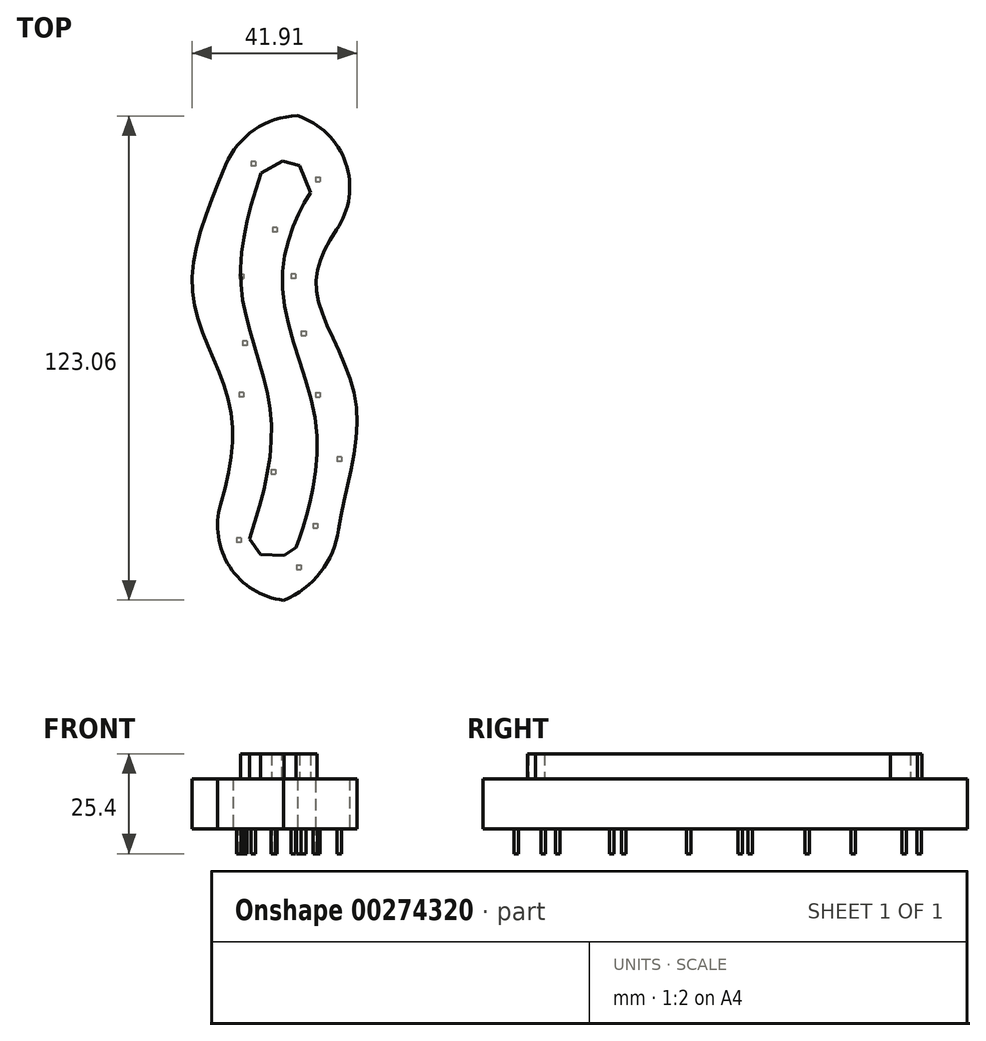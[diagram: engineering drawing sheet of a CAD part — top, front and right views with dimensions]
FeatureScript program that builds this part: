
annotation { "Feature Type Name" : "Feature", "Feature Type Description" : "" }
export const myFeature = defineFeature(function(context is Context, id is Id, definition is map)
    precondition{}
    {
        {
            var Q0;
            Q0=qCreatedBy(makeId("Top.planeOp"),FACE);
            var sketch = newSketch(context, id + "F0", { "sketchPlane" : qUnion([Q0])});
            skFitSpline(sketch, "E0", {"points": [v(-41.01, -54.79) * mm, v(-30.73, -10.92) * mm, v(-40.76, 21.76) * mm, v(-25.89, 69.26) * mm], "startDerivative": vector(46.92, 133.29) * mm, "endDerivative": vector(46.95, 139.93) * mm});
            skLineSegment(sketch, "E1", {"start": v(-25.89, 69.26) * mm, "end": v(10.42, 57.7) * mm});
            skFitSpline(sketch, "E2", {"points": [v(10.42, 57.7) * mm, v(-3.88, 36.84) * mm, v(-9.01, 19.64) * mm, v(0.92, -8.43) * mm, v(-3.91, -43.6) * mm, v(-2.91, -59.33) * mm], "startDerivative": vector(-38.98, -103.6) * mm, "endDerivative": vector(-24.02, -86.28) * mm});
            skLineSegment(sketch, "E3", {"start": v(-41.01, -54.79) * mm, "end": v(-2.91, -59.33) * mm});
            skSolve(sketch);
        }
        {
            var Q0;
            Q0=qCreatedBy(makeId("Top.planeOp"),FACE);
            var sketch = newSketch(context, id + "F1", { "sketchPlane" : qUnion([Q0])});
            skFitSpline(sketch, "E4", {"points": [v(-27.4, -45.76) * mm, v(-20.77, -10.84) * mm, v(-28.3, 21.68) * mm, v(-21.98, 55.1) * mm], "startDerivative": vector(33.82, 104.13) * mm, "endDerivative": vector(33.06, 101.43) * mm});
            skLineSegment(sketch, "E5", {"start": v(-27.4, -45.76) * mm, "end": v(-15.12, -46.35) * mm});
            skLineSegment(sketch, "E6", {"start": v(-21.98, 55.1) * mm, "end": v(-7.23, 51.18) * mm});
            skFitSpline(sketch, "E7", {"points": [v(-7.23, 51.18) * mm, v(-13.75, 40.56) * mm, v(-17.7, 19.75) * mm, v(-9.4, -12.47) * mm, v(-11.83, -36.29) * mm, v(-15.12, -46.35) * mm], "startDerivative": vector(-42.38, -59.93) * mm, "endDerivative": vector(-21.73, -60.8) * mm});
            skSolve(sketch);
        }
        {
            var Q0;
            Q0=makeQuery(id+"F1.imprint","IMPRINT",FACE,{"disambiguationData":[TD([[makeQuery(id+"F1.imprint","IMPRINT",EDGE,{"derivedFrom":sQuery(id+"F1.wireOp",EDGE,"E4")}),-1.0]])]});
            extrude(context, id + "F2", {"entities" : qUnion([Q0]), "depth" : 25.4 * mm});
        }
        {
            var Q0;
            Q0=makeQuery(id+"F0.imprint","IMPRINT",FACE,{"disambiguationData":[TD([[makeQuery(id+"F0.imprint","IMPRINT",EDGE,{"derivedFrom":sQuery(id+"F0.wireOp",EDGE,"E0")}),-1.0]])]});
            extrude(context, id + "F3", {"entities" : qUnion([Q0]), "operationType" : NewBodyOperationType.ADD, "depth" : 12.7 * mm});
        }
        {
            var Q0;
            Q0=makeQuery(id+"F3.boolean.opBoolean","MERGE",FACE,{"derivedFrom":[makeQuery(id+"F2.opExtrude","CAP_FACE",FACE,{"disambiguationData":[OSD([sQuery(id+"F1.wireOp",EDGE,"E4"),sQuery(id+"F1.wireOp",EDGE,"E5"),sQuery(id+"F1.wireOp",EDGE,"E6"),sQuery(id+"F1.wireOp",EDGE,"E7")])],"isStart":true}),makeQuery(id+"F3.opExtrude","CAP_FACE",FACE,{"disambiguationData":[OSD([sQuery(id+"F0.wireOp",EDGE,"E0"),sQuery(id+"F0.wireOp",EDGE,"E1"),sQuery(id+"F0.wireOp",EDGE,"E2"),sQuery(id+"F0.wireOp",EDGE,"E3")])],"isStart":true})]});
            extrude(context, id + "F4", {"entities" : qUnion([Q0]), "operationType" : NewBodyOperationType.REMOVE, "oppositeDirection" : true, "depth" : 6.35 * mm});
        }
        {
            var Q0;
            Q0=makeQuery(id+"F3.opExtrude","CAP_FACE",FACE,{"disambiguationData":[OSD([sQuery(id+"F0.wireOp",EDGE,"E0"),sQuery(id+"F0.wireOp",EDGE,"E1"),sQuery(id+"F0.wireOp",EDGE,"E2"),sQuery(id+"F0.wireOp",EDGE,"E3")])],"isStart":false});
            extrude(context, id + "F5", {"entities" : qUnion([Q0]), "operationType" : NewBodyOperationType.ADD, "depth" : 6.35 * mm});
        }
        {
            var Q0;
            {var subQ0=sQuery(id+"F0.wireOp",EDGE,"E3");var subQ1=sQuery(id+"F0.wireOp",EDGE,"E0");Q0=makeQuery(id+"F5.boolean.opBoolean","MERGE",EDGE,{"derivedFrom":[makeQuery(id+"F3.opExtrude","SWEPT_EDGE",EDGE,{"disambiguationData":[OSD([subQ1,subQ0])]}),makeQuery(id+"F5.opExtrude","SWEPT_EDGE",EDGE,{"disambiguationData":[OSD([subQ1,subQ0])]})]});}
            fillet(context, id + "F6", {"entities" : qUnion([Q0]), "radius" : 19.05 * mm, "tangentPropagation" : true, "allowEdgeOverflow" : false});
        }
        {
            var Q0;
            {var subQ0=sQuery(id+"F0.wireOp",EDGE,"E3");var subQ1=sQuery(id+"F0.wireOp",EDGE,"E2");Q0=makeQuery(id+"F5.boolean.opBoolean","MERGE",EDGE,{"derivedFrom":[makeQuery(id+"F3.opExtrude","SWEPT_EDGE",EDGE,{"disambiguationData":[OSD([subQ1,subQ0])]}),makeQuery(id+"F5.opExtrude","SWEPT_EDGE",EDGE,{"disambiguationData":[OSD([subQ1,subQ0])]})]});}
            fillet(context, id + "F7", {"entities" : qUnion([Q0]), "radius" : 22.86 * mm, "tangentPropagation" : true, "allowEdgeOverflow" : false});
        }
        {
            var Q0;
            {var subQ0=sQuery(id+"F0.wireOp",EDGE,"E2");var subQ1=sQuery(id+"F0.wireOp",EDGE,"E1");Q0=makeQuery(id+"F5.boolean.opBoolean","MERGE",EDGE,{"derivedFrom":[makeQuery(id+"F3.opExtrude","SWEPT_EDGE",EDGE,{"disambiguationData":[OSD([subQ1,subQ0])]}),makeQuery(id+"F5.opExtrude","SWEPT_EDGE",EDGE,{"disambiguationData":[OSD([subQ1,subQ0])]})]});}
            fillet(context, id + "F8", {"entities" : qUnion([Q0]), "radius" : 19.05 * mm, "tangentPropagation" : true, "allowEdgeOverflow" : false});
        }
        {
            var Q0;
            {var subQ0=sQuery(id+"F0.wireOp",EDGE,"E1");var subQ1=sQuery(id+"F0.wireOp",EDGE,"E0");Q0=makeQuery(id+"F5.boolean.opBoolean","MERGE",EDGE,{"derivedFrom":[makeQuery(id+"F3.opExtrude","SWEPT_EDGE",EDGE,{"disambiguationData":[OSD([subQ1,subQ0])]}),makeQuery(id+"F5.opExtrude","SWEPT_EDGE",EDGE,{"disambiguationData":[OSD([subQ1,subQ0])]})]});}
            fillet(context, id + "F9", {"entities" : qUnion([Q0]), "radius" : 20.32 * mm, "tangentPropagation" : true, "allowEdgeOverflow" : false});
        }
        {
            var Q0;
            Q0=makeQuery(id+"F2.opExtrude","SWEPT_EDGE",EDGE,{"disambiguationData":[OSD([sQuery(id+"F1.wireOp",EDGE,"E5"),sQuery(id+"F1.wireOp",EDGE,"E7")])]});
            var Q1;
            Q1=makeQuery(id+"F2.opExtrude","SWEPT_EDGE",EDGE,{"disambiguationData":[OSD([sQuery(id+"F1.wireOp",EDGE,"E4"),sQuery(id+"F1.wireOp",EDGE,"E5")])]});
            chamfer(context, id + "F10", {"entities" : qUnion([Q0, Q1]), "width" : 3.05 * mm, "tangentPropagation" : true});
        }
        {
            var Q0;
            Q0=makeQuery(id+"F2.opExtrude","SWEPT_EDGE",EDGE,{"disambiguationData":[OSD([sQuery(id+"F1.wireOp",EDGE,"E4"),sQuery(id+"F1.wireOp",EDGE,"E6")])]});
            var Q1;
            Q1=makeQuery(id+"F2.opExtrude","SWEPT_EDGE",EDGE,{"disambiguationData":[OSD([sQuery(id+"F1.wireOp",EDGE,"E6"),sQuery(id+"F1.wireOp",EDGE,"E7")])]});
            chamfer(context, id + "F11", {"entities" : qUnion([Q0, Q1]), "width" : 4.57 * mm, "tangentPropagation" : true});
        }
        {
            var Q0;
            Q0=makeQuery(id+"F4.boolean.opBoolean","COPY",FACE,{"derivedFrom":makeQuery(id+"F4.opExtrude","CAP_FACE",FACE,{"disambiguationData":[OSD([sQuery(id+"F0.wireOp",EDGE,"E0"),sQuery(id+"F0.wireOp",EDGE,"E1"),sQuery(id+"F0.wireOp",EDGE,"E2"),sQuery(id+"F0.wireOp",EDGE,"E3"),sQuery(id+"F1.wireOp",EDGE,"E4"),sQuery(id+"F1.wireOp",EDGE,"E5"),sQuery(id+"F1.wireOp",EDGE,"E6"),sQuery(id+"F1.wireOp",EDGE,"E7")])],"isStart":false})});
            var sketch = newSketch(context, id + "F12", { "sketchPlane" : qUnion([Q0])});
            skLineSegment(sketch, "E8.bottom", {"start": v(-14.22, 48.6) * mm, "end": v(-13.08, 48.6) * mm});
            skLineSegment(sketch, "E8.top", {"start": v(-14.22, 49.74) * mm, "end": v(-13.08, 49.74) * mm});
            skLineSegment(sketch, "E8.left", {"start": v(-14.22, 48.6) * mm, "end": v(-14.22, 49.74) * mm});
            skLineSegment(sketch, "E8.right", {"start": v(-13.08, 48.6) * mm, "end": v(-13.08, 49.74) * mm});
            skPoint(sketch, "E8.middle", {"position": v(-13.65, 49.17) * mm});
            skLineSegment(sketch, "E9.bottom", {"start": v(-28.31, 41.74) * mm, "end": v(-29.45, 41.74) * mm});
            skLineSegment(sketch, "E9.top", {"start": v(-28.31, 42.88) * mm, "end": v(-29.45, 42.88) * mm});
            skLineSegment(sketch, "E9.left", {"start": v(-28.31, 41.74) * mm, "end": v(-28.31, 42.88) * mm});
            skLineSegment(sketch, "E9.right", {"start": v(-29.45, 41.74) * mm, "end": v(-29.45, 42.88) * mm});
            skPoint(sketch, "E9.middle", {"position": v(-28.88, 42.31) * mm});
            skLineSegment(sketch, "E10.bottom", {"start": v(-10.01, 38.08) * mm, "end": v(-8.87, 38.08) * mm});
            skLineSegment(sketch, "E10.top", {"start": v(-10.01, 39.22) * mm, "end": v(-8.87, 39.22) * mm});
            skLineSegment(sketch, "E10.left", {"start": v(-10.01, 38.08) * mm, "end": v(-10.01, 39.22) * mm});
            skLineSegment(sketch, "E10.right", {"start": v(-8.87, 38.08) * mm, "end": v(-8.87, 39.22) * mm});
            skPoint(sketch, "E10.middle", {"position": v(-9.44, 38.65) * mm});
            skLineSegment(sketch, "E11.bottom", {"start": v(-20.72, 24.34) * mm, "end": v(-19.58, 24.34) * mm});
            skLineSegment(sketch, "E11.top", {"start": v(-20.72, 25.48) * mm, "end": v(-19.58, 25.48) * mm});
            skLineSegment(sketch, "E11.left", {"start": v(-20.72, 24.34) * mm, "end": v(-20.72, 25.48) * mm});
            skLineSegment(sketch, "E11.right", {"start": v(-19.58, 24.34) * mm, "end": v(-19.58, 25.48) * mm});
            skPoint(sketch, "E11.middle", {"position": v(-20.15, 24.91) * mm});
            skLineSegment(sketch, "E12.bottom", {"start": v(-2.85, 21.25) * mm, "end": v(-4, 21.25) * mm});
            skLineSegment(sketch, "E12.top", {"start": v(-2.85, 22.4) * mm, "end": v(-4, 22.4) * mm});
            skLineSegment(sketch, "E12.left", {"start": v(-2.85, 21.25) * mm, "end": v(-2.85, 22.4) * mm});
            skLineSegment(sketch, "E12.right", {"start": v(-4, 21.25) * mm, "end": v(-4, 22.4) * mm});
            skPoint(sketch, "E12.middle", {"position": v(-3.42, 21.82) * mm});
            skLineSegment(sketch, "E13.bottom", {"start": v(-9.44, 4.77) * mm, "end": v(-8.3, 4.77) * mm});
            skLineSegment(sketch, "E13.top", {"start": v(-9.44, 5.91) * mm, "end": v(-8.3, 5.91) * mm});
            skLineSegment(sketch, "E13.left", {"start": v(-9.44, 4.77) * mm, "end": v(-9.44, 5.91) * mm});
            skLineSegment(sketch, "E13.right", {"start": v(-8.3, 4.77) * mm, "end": v(-8.3, 5.91) * mm});
            skPoint(sketch, "E13.middle", {"position": v(-8.87, 5.34) * mm});
            skLineSegment(sketch, "E14.bottom", {"start": v(-27.74, 4.77) * mm, "end": v(-28.88, 4.77) * mm});
            skLineSegment(sketch, "E14.top", {"start": v(-27.74, 5.91) * mm, "end": v(-28.88, 5.91) * mm});
            skLineSegment(sketch, "E14.left", {"start": v(-27.74, 4.77) * mm, "end": v(-27.74, 5.91) * mm});
            skLineSegment(sketch, "E14.right", {"start": v(-28.88, 4.77) * mm, "end": v(-28.88, 5.91) * mm});
            skPoint(sketch, "E14.middle", {"position": v(-28.31, 5.34) * mm});
            skLineSegment(sketch, "E15.bottom", {"start": v(-13.14, -12.39) * mm, "end": v(-11.88, -12.39) * mm});
            skLineSegment(sketch, "E15.top", {"start": v(-13.14, -9.72) * mm, "end": v(-11.88, -9.72) * mm});
            skLineSegment(sketch, "E15.left", {"start": v(-13.14, -12.39) * mm, "end": v(-13.14, -9.72) * mm});
            skLineSegment(sketch, "E15.right", {"start": v(-11.88, -12.39) * mm, "end": v(-11.88, -9.72) * mm});
            skPoint(sketch, "E15.middle", {"position": v(-12.5, -11.05) * mm});
            skPoint(sketch, "E16.middle", {"position": v(-34.5, -5.78) * mm});
            skLineSegment(sketch, "E17.bottom", {"start": v(-14.56, -25.3) * mm, "end": v(-15.7, -25.3) * mm});
            skLineSegment(sketch, "E17.top", {"start": v(-14.56, -24.17) * mm, "end": v(-15.7, -24.17) * mm});
            skLineSegment(sketch, "E17.left", {"start": v(-14.56, -25.3) * mm, "end": v(-14.56, -24.17) * mm});
            skLineSegment(sketch, "E17.right", {"start": v(-15.7, -25.3) * mm, "end": v(-15.7, -24.17) * mm});
            skPoint(sketch, "E17.middle", {"position": v(-15.13, -24.74) * mm});
            skLineSegment(sketch, "E18.bottom", {"start": v(-28.31, -24.74) * mm, "end": v(-28.31, -24.74) * mm});
            skLineSegment(sketch, "E19.bottom", {"start": v(-19.2, -37.1) * mm, "end": v(-20.34, -37.1) * mm});
            skLineSegment(sketch, "E19.top", {"start": v(-19.2, -35.95) * mm, "end": v(-20.34, -35.95) * mm});
            skLineSegment(sketch, "E19.left", {"start": v(-19.2, -37.1) * mm, "end": v(-19.2, -35.95) * mm});
            skLineSegment(sketch, "E19.right", {"start": v(-20.34, -37.1) * mm, "end": v(-20.34, -35.95) * mm});
            skPoint(sketch, "E19.middle", {"position": v(-19.77, -36.53) * mm});
            skLineSegment(sketch, "E20.bottom", {"start": v(-9.44, -49.98) * mm, "end": v(-8.3, -49.98) * mm});
            skLineSegment(sketch, "E20.top", {"start": v(-9.44, -48.83) * mm, "end": v(-8.3, -48.83) * mm});
            skLineSegment(sketch, "E20.left", {"start": v(-9.44, -49.98) * mm, "end": v(-9.44, -48.83) * mm});
            skLineSegment(sketch, "E20.right", {"start": v(-8.3, -49.98) * mm, "end": v(-8.3, -48.83) * mm});
            skPoint(sketch, "E20.middle", {"position": v(-8.87, -49.4) * mm});
            skLineSegment(sketch, "E21.bottom", {"start": v(-24.7, -53.8) * mm, "end": v(-25.84, -53.8) * mm});
            skLineSegment(sketch, "E21.top", {"start": v(-24.7, -52.66) * mm, "end": v(-25.84, -52.66) * mm});
            skLineSegment(sketch, "E21.left", {"start": v(-24.7, -53.8) * mm, "end": v(-24.7, -52.66) * mm});
            skLineSegment(sketch, "E21.right", {"start": v(-25.84, -53.8) * mm, "end": v(-25.84, -52.66) * mm});
            skPoint(sketch, "E21.middle", {"position": v(-25.27, -53.23) * mm});
            skLineSegment(sketch, "E22.bottom", {"start": v(-26.8, -8.28) * mm, "end": v(-27.94, -8.28) * mm});
            skLineSegment(sketch, "E22.top", {"start": v(-26.8, -7.13) * mm, "end": v(-27.94, -7.13) * mm});
            skLineSegment(sketch, "E22.left", {"start": v(-26.8, -8.28) * mm, "end": v(-26.8, -7.13) * mm});
            skLineSegment(sketch, "E22.right", {"start": v(-27.94, -8.28) * mm, "end": v(-27.94, -7.13) * mm});
            skPoint(sketch, "E22.middle", {"position": v(-27.37, -7.7) * mm});
            skLineSegment(sketch, "E23.bottom", {"start": v(-28.88, -25.3) * mm, "end": v(-27.74, -25.3) * mm});
            skLineSegment(sketch, "E23.top", {"start": v(-28.88, -24.17) * mm, "end": v(-27.74, -24.17) * mm});
            skLineSegment(sketch, "E23.left", {"start": v(-28.88, -25.3) * mm, "end": v(-28.88, -24.17) * mm});
            skLineSegment(sketch, "E23.right", {"start": v(-27.74, -25.3) * mm, "end": v(-27.74, -24.17) * mm});
            skPoint(sketch, "E23.middle", {"position": v(-28.31, -24.74) * mm});
            skSolve(sketch);
        }
        {
            var Q0;
            Q0=makeQuery(id+"F12.imprint","IMPRINT",FACE,{"disambiguationData":[TD([[makeQuery(id+"F12.imprint","IMPRINT",EDGE,{"derivedFrom":sQuery(id+"F12.wireOp",EDGE,"E9.bottom")}),-1.0]])]});
            var Q1;
            Q1=makeQuery(id+"F12.imprint","IMPRINT",FACE,{"disambiguationData":[TD([[makeQuery(id+"F12.imprint","IMPRINT",EDGE,{"derivedFrom":sQuery(id+"F12.wireOp",EDGE,"E8.bottom")}),1.0]])]});
            var Q2;
            Q2=makeQuery(id+"F12.imprint","IMPRINT",FACE,{"disambiguationData":[TD([[makeQuery(id+"F12.imprint","IMPRINT",EDGE,{"derivedFrom":sQuery(id+"F12.wireOp",EDGE,"E10.bottom")}),1.0]])]});
            var Q3;
            Q3=makeQuery(id+"F12.imprint","IMPRINT",FACE,{"disambiguationData":[TD([[makeQuery(id+"F12.imprint","IMPRINT",EDGE,{"derivedFrom":sQuery(id+"F12.wireOp",EDGE,"E12.bottom")}),-1.0]])]});
            var Q4;
            Q4=makeQuery(id+"F12.imprint","IMPRINT",FACE,{"disambiguationData":[TD([[makeQuery(id+"F12.imprint","IMPRINT",EDGE,{"derivedFrom":sQuery(id+"F12.wireOp",EDGE,"E13.bottom")}),1.0]])]});
            var Q5;
            Q5=makeQuery(id+"F12.imprint","IMPRINT",FACE,{"disambiguationData":[TD([[makeQuery(id+"F12.imprint","IMPRINT",EDGE,{"derivedFrom":sQuery(id+"F12.wireOp",EDGE,"E11.bottom")}),1.0]])]});
            var Q6;
            Q6=makeQuery(id+"F12.imprint","IMPRINT",FACE,{"disambiguationData":[TD([[makeQuery(id+"F12.imprint","IMPRINT",EDGE,{"derivedFrom":sQuery(id+"F12.wireOp",EDGE,"E14.bottom")}),-1.0]])]});
            var Q7;
            Q7=makeQuery(id+"F12.imprint","IMPRINT",FACE,{"disambiguationData":[TD([[makeQuery(id+"F12.imprint","IMPRINT",EDGE,{"derivedFrom":sQuery(id+"F12.wireOp",EDGE,"E22.bottom")}),-1.0]])]});
            var Q8;
            Q8=makeQuery(id+"F12.imprint","IMPRINT",FACE,{"disambiguationData":[TD([[makeQuery(id+"F12.imprint","IMPRINT",EDGE,{"derivedFrom":sQuery(id+"F12.wireOp",EDGE,"E15.bottom")}),1.0]])]});
            var Q9;
            Q9=makeQuery(id+"F12.imprint","IMPRINT",FACE,{"disambiguationData":[TD([[makeQuery(id+"F12.imprint","IMPRINT",EDGE,{"derivedFrom":sQuery(id+"F12.wireOp",EDGE,"E17.bottom")}),-1.0]])]});
            var Q10;
            Q10=makeQuery(id+"F12.imprint","IMPRINT",FACE,{"disambiguationData":[TD([[makeQuery(id+"F12.imprint","IMPRINT",EDGE,{"derivedFrom":sQuery(id+"F12.wireOp",EDGE,"E19.bottom")}),-1.0]])]});
            var Q11;
            Q11=makeQuery(id+"F12.imprint","IMPRINT",FACE,{"disambiguationData":[TD([[makeQuery(id+"F12.imprint","IMPRINT",EDGE,{"derivedFrom":sQuery(id+"F12.wireOp",EDGE,"E23.bottom")}),1.0]])]});
            var Q12;
            Q12=makeQuery(id+"F12.imprint","IMPRINT",FACE,{"disambiguationData":[TD([[makeQuery(id+"F12.imprint","IMPRINT",EDGE,{"derivedFrom":sQuery(id+"F12.wireOp",EDGE,"E20.bottom")}),1.0]])]});
            var Q13;
            Q13=makeQuery(id+"F12.imprint","IMPRINT",FACE,{"disambiguationData":[TD([[makeQuery(id+"F12.imprint","IMPRINT",EDGE,{"derivedFrom":sQuery(id+"F12.wireOp",EDGE,"E21.bottom")}),-1.0]])]});
            extrude(context, id + "F13", {"entities" : qUnion([Q0, Q1, Q2, Q3, Q4, Q5, Q6, Q7, Q8, Q9, Q10, Q11, Q12, Q13]), "operationType" : NewBodyOperationType.ADD, "depth" : 6.35 * mm});
        }
        {
            var Q0;
            Q0=makeQuery(id+"F13.opExtrude","SWEPT_FACE",FACE,{"disambiguationData":[OSD([sQuery(id+"F12.wireOp",EDGE,"E15.bottom")])]});
            extrude(context, id + "F14", {"entities" : qUnion([Q0]), "operationType" : NewBodyOperationType.REMOVE, "oppositeDirection" : true, "depth" : 1.52 * mm});
        }
    });
